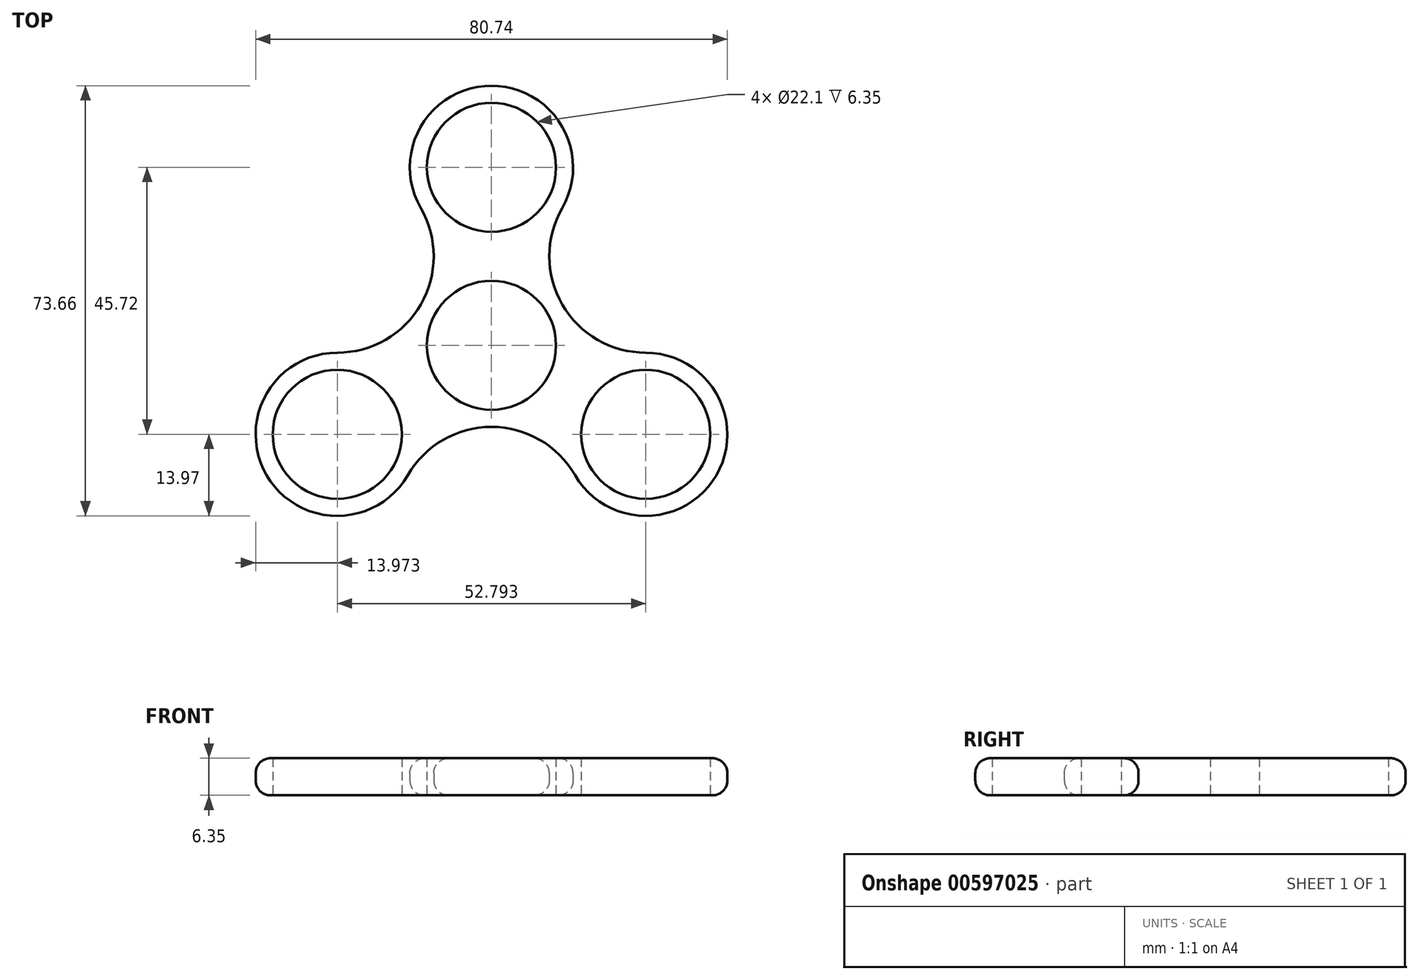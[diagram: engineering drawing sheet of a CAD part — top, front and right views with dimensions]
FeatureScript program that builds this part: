
annotation { "Feature Type Name" : "Feature", "Feature Type Description" : "" }
export const myFeature = defineFeature(function(context is Context, id is Id, definition is map)
    precondition{}
    {
        {
            var Q0;
            Q0=qCreatedBy(makeId("Top.planeOp"),FACE);
            var sketch = newSketch(context, id + "F0", { "sketchPlane" : qUnion([Q0])});
            skCircle(sketch, "E0", {"center": v(0, 0) * mm, "radius": 11.05 * mm});
            skCircle(sketch, "E1", {"center": v(0, 0) * mm, "radius": 13.97 * mm});
            skLineSegment(sketch, "E2", {"start": v(0, 0) * mm, "end": v(0, 30.48) * mm});
            skCircle(sketch, "E3", {"center": v(0, 30.48) * mm, "radius": 11.05 * mm});
            skCircle(sketch, "E4", {"center": v(0, 30.48) * mm, "radius": 13.97 * mm});
            skCircle(sketch, "E5.1.0", {"center": v(-26.4, -15.24) * mm, "radius": 11.05 * mm});
            skCircle(sketch, "E5.1.1", {"center": v(-26.4, -15.24) * mm, "radius": 13.97 * mm});
            skCircle(sketch, "E5.2.0", {"center": v(26.4, -15.24) * mm, "radius": 11.05 * mm});
            skCircle(sketch, "E5.2.1", {"center": v(26.4, -15.24) * mm, "radius": 13.97 * mm});
            skLineSegment(sketch, "E6", {"start": v(0, 0) * mm, "end": v(-26.4, 15.24) * mm});
            skArc(sketch, "E7", {"start": v(-26.4, -1.27) * mm, "mid": v(-12.1, 6.99) * mm, "end": v(-12.1, 23.5) * mm});
            skArc(sketch, "E8.1.0", {"start": v(14.3, -22.23) * mm, "mid": v(0, -13.97) * mm, "end": v(-14.3, -22.22) * mm});
            skArc(sketch, "E8.2.0", {"start": v(12.1, 23.5) * mm, "mid": v(12.1, 6.98) * mm, "end": v(26.4, -1.27) * mm});
            skSolve(sketch);
        }
        {
            var Q0;
            Q0 = qSketchRegion(id + "F0", true);
            extrude(context, id + "F1", {"entities" : qUnion([Q0]), "depth" : 6.35 * mm, "offsetDistance" : 25.4 * mm});
        }
        {
            var Q0;
            Q0=makeQuery(id+"F1.opExtrude","CAP_EDGE",EDGE,{"disambiguationData":[OSD([sQuery(id+"F0.wireOp",EDGE,"E8.1.0")])],"isStart":false});
            var Q1;
            Q1=makeQuery(id+"F1.opExtrude","CAP_EDGE",EDGE,{"disambiguationData":[OSD([sQuery(id+"F0.wireOp",EDGE,"E8.1.0")])],"isStart":true});
            fillet(context, id + "F2", {"entities" : qUnion([Q0, Q1]), "radius" : 2.54 * mm, "tangentPropagation" : true, "allowEdgeOverflow" : false});
        }
    });
